# Revit family: QF_BOURGEAT_tables_de_tri_hauteur_rabaissée_primaire_2TVO
name_source: partatom
category: Equipement spécialisé
revit_build: Autodesk Revit 2015 (Build: 20140606_1530(x64)
units: mm (PartAtom-declared; Revit-internal decimal feet)

## types (3) — shared parameters
Décalage du sol = 27 mm  [stored 0.0885827 ft]
Fabricant = BOURGEAT
Hauteur hors tout = 700 mm  [stored 2.29659 ft]
Inox = Acier inoxydable, poli
Longueur hors tout = 1030 mm  [stored 3.37927 ft]
Panneaux = PVC, non plastifié
Pieds = Oui
Spécification du Fabricant = Table de collecte et de tri hauteur rabaissée primaire
URL catalogue = http://www.bourgeat.fr

## per-type parameters (varying)
| type | Avec panneaux | Modèle | Poids net à vide | Profondeur hors tout | Rampe |
| Sans rampe - Sans panneaux - Avec pieds | Non | 859002 | 29.00 kg | 600 mm | Non |
| Avec rampe - Sans panneaux - Avec pieds | Non | 859022 | 32.00 kg | 850 mm  [stored 2.78871 ft] | Oui |
| Avec rampe - Avec panneaux - Avec pieds | Oui | 859102 | 32.00 kg | 850 mm  [stored 2.78871 ft] | Oui |

note: [stored X ft] marks values corroborated as IEEE doubles in the binary element streams (Revit-internal decimal feet)

## geometry (parser evidence)
native form markers: Blend x12
no freeform markers — native parametric forms only
